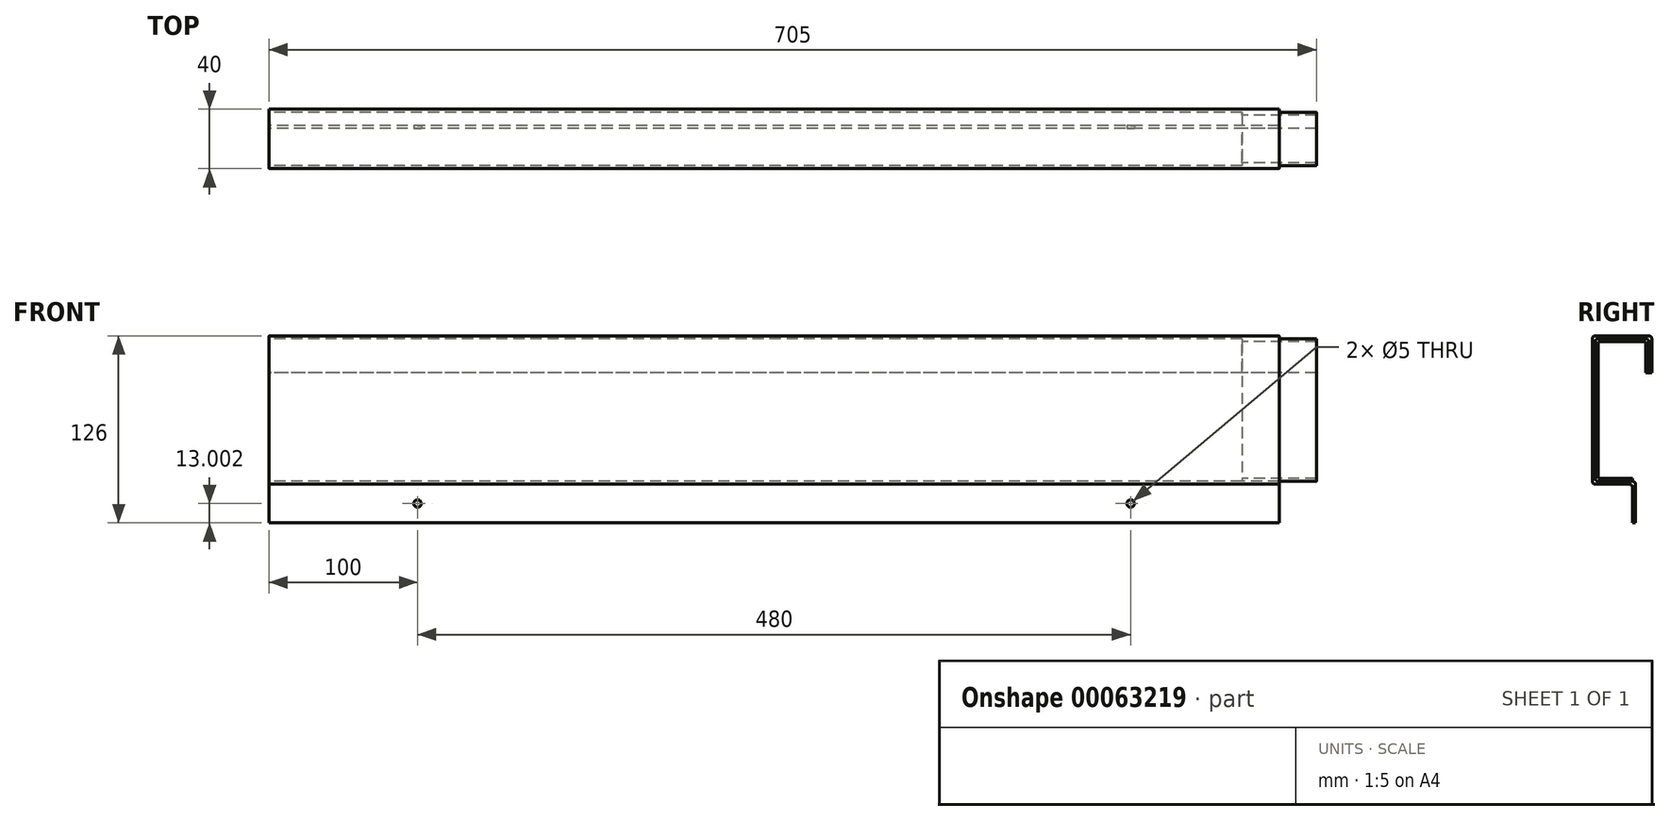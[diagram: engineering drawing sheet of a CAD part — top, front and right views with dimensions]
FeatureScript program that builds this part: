
annotation { "Feature Type Name" : "Feature", "Feature Type Description" : "" }
export const myFeature = defineFeature(function(context is Context, id is Id, definition is map)
    precondition{}
    {
        {
            var Q0;
            Q0=qCreatedBy(makeId("Right.planeOp"),FACE);
            var sketch = newSketch(context, id + "F0", { "sketchPlane" : qUnion([Q0])});
            skLineSegment(sketch, "E0", {"start": v(0, 0) * mm, "end": v(0, 430) * mm, "construction": true});
            skLineSegment(sketch, "E1", {"start": v(0, 0) * mm, "end": v(-250, 0) * mm, "construction": true});
            skLineSegment(sketch, "E2", {"start": v(-18.84, 154.8) * mm, "end": v(-18.84, 177.8) * mm});
            skLineSegment(sketch, "E3", {"start": v(-18.84, 177.8) * mm, "end": v(-54.84, 177.8) * mm});
            skLineSegment(sketch, "E4", {"start": v(-54.84, 177.8) * mm, "end": v(-54.84, 81.8) * mm});
            skLineSegment(sketch, "E5", {"start": v(-54.84, 81.8) * mm, "end": v(-27.84, 81.8) * mm});
            skLineSegment(sketch, "E6.0", {"start": v(-56.84, 79.8) * mm, "end": v(-29.84, 79.8) * mm});
            skLineSegment(sketch, "E6.1", {"start": v(-56.84, 179.8) * mm, "end": v(-56.84, 79.8) * mm});
            skLineSegment(sketch, "E6.2", {"start": v(-16.84, 179.8) * mm, "end": v(-56.84, 179.8) * mm});
            skLineSegment(sketch, "E6.3", {"start": v(-16.84, 154.8) * mm, "end": v(-16.84, 179.8) * mm});
            skLineSegment(sketch, "E7", {"start": v(-27.84, 81.8) * mm, "end": v(-27.84, 53.8) * mm});
            skLineSegment(sketch, "E8", {"start": v(-29.84, 79.8) * mm, "end": v(-29.84, 53.8) * mm});
            skLineSegment(sketch, "E9", {"start": v(-16.84, 154.8) * mm, "end": v(-18.84, 154.8) * mm});
            skLineSegment(sketch, "E10", {"start": v(-27.84, 53.8) * mm, "end": v(-29.84, 53.8) * mm});
            skSolve(sketch);
        }
        {
            var Q0;
            Q0=makeQuery(id+"F0.imprint","IMPRINT",FACE,{"disambiguationData":[TD([[makeQuery(id+"F0.imprint","IMPRINT",EDGE,{"derivedFrom":sQuery(id+"F0.wireOp",EDGE,"97aded3f-c788-494d-ab92-4e00cf807f6c")}),-1.0]])]});
            var Q1;
            Q1=makeQuery(id+"F0.imprint","IMPRINT",FACE,{"disambiguationData":[TD([[makeQuery(id+"F0.imprint","IMPRINT",EDGE,{"derivedFrom":sQuery(id+"F0.wireOp",EDGE,"E2")}),-1.0]])]});
            extrude(context, id + "F1", {"entities" : qUnion([Q0, Q1]), "depth" : 680 * mm});
        }
        {
            var Q0;
            Q0=makeQuery(id+"F1.opExtrude","SWEPT_FACE",FACE,{"disambiguationData":[OSD([sQuery(id+"F0.wireOp",EDGE,"E8")])]});
            var sketch = newSketch(context, id + "F2", { "sketchPlane" : qUnion([Q0])});
            skLineSegment(sketch, "E11", {"start": v(0, 66.8) * mm, "end": v(680, 66.8) * mm});
            skLineSegment(sketch, "E12", {"start": v(580, 79.8) * mm, "end": v(580, 53.8) * mm});
            skPoint(sketch, "E13", {"position": v(580, 66.8) * mm});
            skLineSegment(sketch, "E14", {"start": v(100, 79.8) * mm, "end": v(100, 53.8) * mm});
            skPoint(sketch, "E15", {"position": v(100, 66.8) * mm});
            skSolve(sketch);
        }
        {
            var Q0;
            Q0=sQuery(id+"F2.wireOp",VERTEX,"497ec98f-e9a9-425a-b2b5-6f80ccc2b2cc");
            var Q1;
            Q1=sQuery(id+"F2.wireOp",VERTEX,"82ee78c0-7a07-4074-a8d9-4abe993744e3");
            var Q2;
            Q2=sQuery(id+"F2.wireOp",VERTEX,"E13");
            var Q3;
            Q3=sQuery(id+"F2.wireOp",VERTEX,"E15");
            var Q4;
            Q4=makeQuery(id+"F1.opExtrude","SWEPT_BODY",BODY,{"disambiguationData":[OSD([sQuery(id+"F0.wireOp",EDGE,"E2"),sQuery(id+"F0.wireOp",EDGE,"E3"),sQuery(id+"F0.wireOp",EDGE,"E4"),sQuery(id+"F0.wireOp",EDGE,"E5"),sQuery(id+"F0.wireOp",EDGE,"E6.0"),sQuery(id+"F0.wireOp",EDGE,"E6.1"),sQuery(id+"F0.wireOp",EDGE,"E6.2"),sQuery(id+"F0.wireOp",EDGE,"E6.3"),sQuery(id+"F0.wireOp",EDGE,"E7"),sQuery(id+"F0.wireOp",EDGE,"E8"),sQuery(id+"F0.wireOp",EDGE,"E9"),sQuery(id+"F0.wireOp",EDGE,"E10")])]});
            hole(context, id + "F3", {"style" : HoleStyle.SIMPLE, "holeDiameter" : 5 * mm, "endStyle" : HoleEndStyle.THROUGH, "locations" : qUnion([Q0, Q1, Q2, Q3]), "scope" : qUnion([Q4])});
        }
        {
            var Q0;
            Q0=makeQuery(id+"F1.opExtrude","SWEPT_EDGE",EDGE,{"disambiguationData":[OSD([sQuery(id+"F0.wireOp",EDGE,"E6.1"),sQuery(id+"F0.wireOp",EDGE,"E6.2")])]});
            var Q1;
            Q1=makeQuery(id+"F1.opExtrude","SWEPT_EDGE",EDGE,{"disambiguationData":[OSD([sQuery(id+"F0.wireOp",EDGE,"E6.2"),sQuery(id+"F0.wireOp",EDGE,"E6.3")])]});
            var Q2;
            Q2=makeQuery(id+"F1.opExtrude","SWEPT_EDGE",EDGE,{"disambiguationData":[OSD([sQuery(id+"F0.wireOp",EDGE,"E6.0"),sQuery(id+"F0.wireOp",EDGE,"E6.1")])]});
            var Q3;
            Q3=makeQuery(id+"F1.opExtrude","SWEPT_EDGE",EDGE,{"disambiguationData":[OSD([sQuery(id+"F0.wireOp",EDGE,"E5"),sQuery(id+"F0.wireOp",EDGE,"E7")])]});
            var Q4;
            Q4=makeQuery(id+"F1.opExtrude","SWEPT_EDGE",EDGE,{"disambiguationData":[OSD([sQuery(id+"F0.wireOp",EDGE,"E4"),sQuery(id+"F0.wireOp",EDGE,"E5")])]});
            var Q5;
            Q5=makeQuery(id+"F1.opExtrude","SWEPT_EDGE",EDGE,{"disambiguationData":[OSD([sQuery(id+"F0.wireOp",EDGE,"E6.0"),sQuery(id+"F0.wireOp",EDGE,"E8")])]});
            var Q6;
            Q6=makeQuery(id+"F1.opExtrude","SWEPT_EDGE",EDGE,{"disambiguationData":[OSD([sQuery(id+"F0.wireOp",EDGE,"E2"),sQuery(id+"F0.wireOp",EDGE,"E3")])]});
            var Q7;
            Q7=makeQuery(id+"F1.opExtrude","SWEPT_EDGE",EDGE,{"disambiguationData":[OSD([sQuery(id+"F0.wireOp",EDGE,"E3"),sQuery(id+"F0.wireOp",EDGE,"E4")])]});
            fillet(context, id + "F4", {"entities" : qUnion([Q0, Q1, Q2, Q3, Q4, Q5, Q6, Q7]), "radius" : 2 * mm, "tangentPropagation" : true, "allowEdgeOverflow" : false});
        }
        {
            var Q0;
            Q0=makeQuery(id+"F1.opExtrude","CAP_FACE",FACE,{"disambiguationData":[OSD([sQuery(id+"F0.wireOp",EDGE,"E2"),sQuery(id+"F0.wireOp",EDGE,"E3"),sQuery(id+"F0.wireOp",EDGE,"E4"),sQuery(id+"F0.wireOp",EDGE,"E5"),sQuery(id+"F0.wireOp",EDGE,"E6.0"),sQuery(id+"F0.wireOp",EDGE,"E6.1"),sQuery(id+"F0.wireOp",EDGE,"E6.2"),sQuery(id+"F0.wireOp",EDGE,"E6.3"),sQuery(id+"F0.wireOp",EDGE,"E7"),sQuery(id+"F0.wireOp",EDGE,"E8"),sQuery(id+"F0.wireOp",EDGE,"E9"),sQuery(id+"F0.wireOp",EDGE,"E10")])],"isStart":false});
            var sketch = newSketch(context, id + "F5", { "sketchPlane" : qUnion([Q0])});
            skLineSegment(sketch, "E16.0.0", {"start": v(-16.84, 154.8) * mm, "end": v(-16.84, 177.8) * mm});
            skArc(sketch, "E16.0.1", {"start": v(-16.84, 177.8) * mm, "mid": v(-17.42, 179.22) * mm, "end": v(-18.84, 179.8) * mm});
            skLineSegment(sketch, "E16.0.2", {"start": v(-18.84, 179.8) * mm, "end": v(-54.84, 179.8) * mm});
            skArc(sketch, "E16.0.3", {"start": v(-54.84, 179.8) * mm, "mid": v(-56.25, 179.22) * mm, "end": v(-56.84, 177.8) * mm});
            skLineSegment(sketch, "E16.0.4", {"start": v(-56.84, 177.8) * mm, "end": v(-56.84, 81.8) * mm});
            skArc(sketch, "E16.0.5", {"start": v(-56.84, 81.8) * mm, "mid": v(-56.25, 80.39) * mm, "end": v(-54.84, 79.8) * mm});
            skLineSegment(sketch, "E16.0.6", {"start": v(-54.84, 79.8) * mm, "end": v(-31.84, 79.8) * mm});
            skArc(sketch, "E16.0.7", {"start": v(-31.84, 79.8) * mm, "mid": v(-30.42, 79.22) * mm, "end": v(-29.84, 77.8) * mm});
            skLineSegment(sketch, "E16.0.8", {"start": v(-29.84, 77.8) * mm, "end": v(-29.84, 53.8) * mm});
            skLineSegment(sketch, "E16.0.9", {"start": v(-29.84, 53.8) * mm, "end": v(-27.84, 53.8) * mm});
            skLineSegment(sketch, "E16.0.10", {"start": v(-27.84, 53.8) * mm, "end": v(-27.84, 79.8) * mm});
            skArc(sketch, "E16.0.11", {"start": v(-27.84, 79.8) * mm, "mid": v(-28.42, 81.22) * mm, "end": v(-29.84, 81.8) * mm});
            skLineSegment(sketch, "E16.0.12", {"start": v(-29.84, 81.8) * mm, "end": v(-52.84, 81.8) * mm});
            skArc(sketch, "E16.0.13", {"start": v(-52.84, 81.8) * mm, "mid": v(-54.25, 82.39) * mm, "end": v(-54.84, 83.8) * mm});
            skLineSegment(sketch, "E16.0.14", {"start": v(-54.84, 83.8) * mm, "end": v(-54.84, 175.8) * mm});
            skArc(sketch, "E16.0.15", {"start": v(-54.84, 175.8) * mm, "mid": v(-54.25, 177.22) * mm, "end": v(-52.84, 177.8) * mm});
            skLineSegment(sketch, "E16.0.16", {"start": v(-52.84, 177.8) * mm, "end": v(-20.84, 177.8) * mm});
            skArc(sketch, "E16.0.17", {"start": v(-20.84, 177.8) * mm, "mid": v(-19.42, 177.22) * mm, "end": v(-18.84, 175.8) * mm});
            skLineSegment(sketch, "E16.0.18", {"start": v(-18.84, 175.8) * mm, "end": v(-18.84, 154.8) * mm});
            skLineSegment(sketch, "E16.0.19", {"start": v(-18.84, 154.8) * mm, "end": v(-16.84, 154.8) * mm});
            skLineSegment(sketch, "E17.0", {"start": v(-20.84, 175.8) * mm, "end": v(-20.84, 154.8) * mm});
            skLineSegment(sketch, "E17.1", {"start": v(-52.84, 175.8) * mm, "end": v(-20.84, 175.8) * mm});
            skLineSegment(sketch, "E17.2", {"start": v(-52.84, 83.8) * mm, "end": v(-52.84, 175.8) * mm});
            skLineSegment(sketch, "E17.3", {"start": v(-29.84, 83.8) * mm, "end": v(-52.84, 83.8) * mm});
            skLineSegment(sketch, "E18", {"start": v(-29.84, 83.8) * mm, "end": v(-29.84, 81.8) * mm});
            skLineSegment(sketch, "E19", {"start": v(-20.84, 154.8) * mm, "end": v(-18.84, 154.8) * mm});
            skSolve(sketch);
        }
        {
            var Q0;
            Q0=makeQuery(id+"F5.imprint","IMPRINT",FACE,{"disambiguationData":[TD([[makeQuery(id+"F5.imprint","IMPRINT",EDGE,{"derivedFrom":sQuery(id+"F5.wireOp",EDGE,"E16.0.12")}),1.0]])]});
            extrude(context, id + "F6", {"entities" : qUnion([Q0]), "operationType" : NewBodyOperationType.ADD, "depth" : 25 * mm, "hasSecondDirection" : true, "secondDirectionOppositeDirection" : true, "secondDirectionDepth" : 25 * mm});
        }
    });
